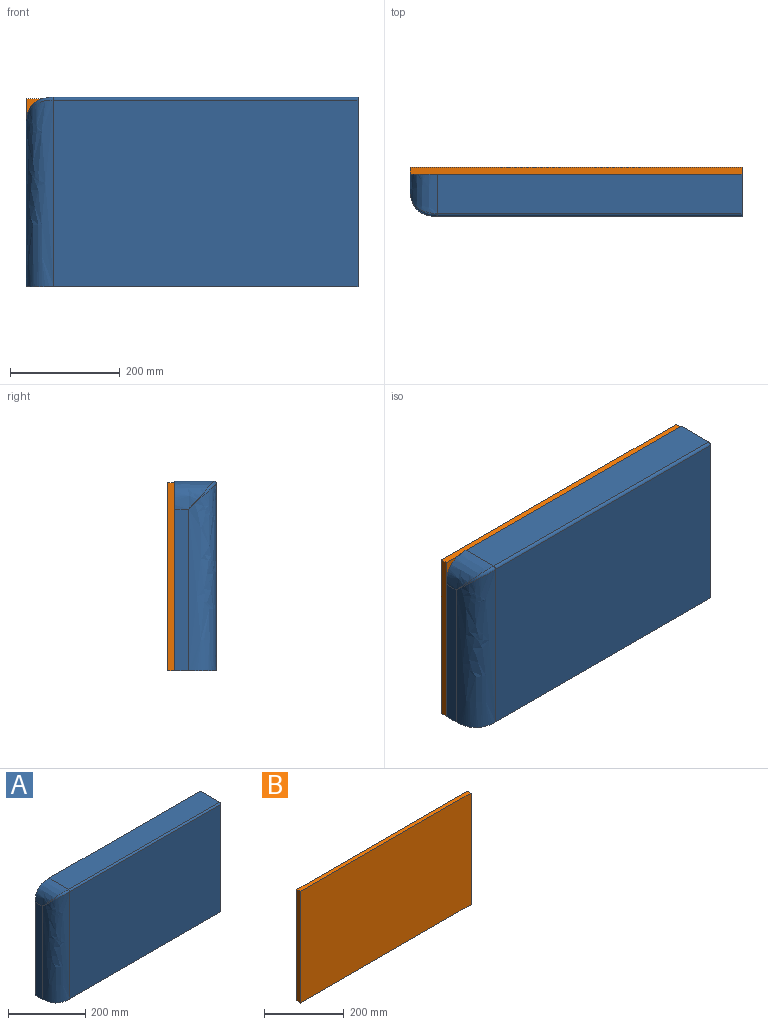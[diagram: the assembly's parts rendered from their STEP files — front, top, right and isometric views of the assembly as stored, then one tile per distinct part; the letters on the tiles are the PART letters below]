
ASSEMBLY  parts=2 mates=1
PART A: 10 faces, bbox 605.2x79.8x362.5 mm
  f0: plane 605.16x76.2mm, normal (0,0,-1), area 45682.7mm2, adj f1,f3,f4,f5,f7
  f1: plane 345.44x76.2mm, normal (1,0,0), area 26317mm2, adj f0,f2,f4,f5,f6
  f2: plane 554.36x71.12mm, normal (0,0,1), area 39425.7mm2, adj f1,f5,f6,f8
  f3: plane 294.64x25.4mm, normal (-1,0,0), area 7483.9mm2, adj f0,f5,f7,f8
  f4: plane 554.36x340.36mm, normal (0,-1,0), area 188680.3mm2, adj f0,f1,f6,f7
  f5: plane 605.16x345.44mm, normal (0,1,0), area 208614.6mm2, adj f0,f1,f2,f3,f8
  f6: cylinder r=5.08mm len=554.36mm, axis (1,0,0), area 4423.6mm2, adj f1,f2,f4,f9
  f7: bspline ~357.38x50.8mm, area 26796.3mm2, adj f0,f3,f4,f9
  f8: bspline ~74.68x50.8mm, area 4594.8mm2, adj f2,f3,f5,f9
  f9: bspline ~71.36x50.8mm, area 301.6mm2, adj f6,f7,f8
PART B: 6 faces, bbox 605.2x12.7x342.9 mm
  f0: plane 605.16x12.7mm, normal (0,0,-1), area 7685.5mm2, adj f1,f3,f4,f5
  f1: plane 342.9x12.7mm, normal (1,0,0), area 4354.8mm2, adj f0,f2,f4,f5
  f2: plane 605.16x12.7mm, normal (0,0,1), area 7685.5mm2, adj f1,f3,f4,f5
  f3: plane 342.9x12.7mm, normal (-1,0,0), area 4354.8mm2, adj f0,f2,f4,f5
  f4: plane 605.16x342.9mm, normal (0,-1,0), area 207507.6mm2, adj f0,f1,f2,f3
  f5: plane 605.16x342.9mm, normal (0,1,0), area 207507.6mm2, adj f0,f1,f2,f3
PLACE A t=(-84.43,-67.84,3.54)mm
PLACE B t=(-84.43,-55.14,3.54)mm
MATE fastened B.f4 <-> A.f5  axis (0,-1,0) through (-84.43,-67.84,3.54)mm
